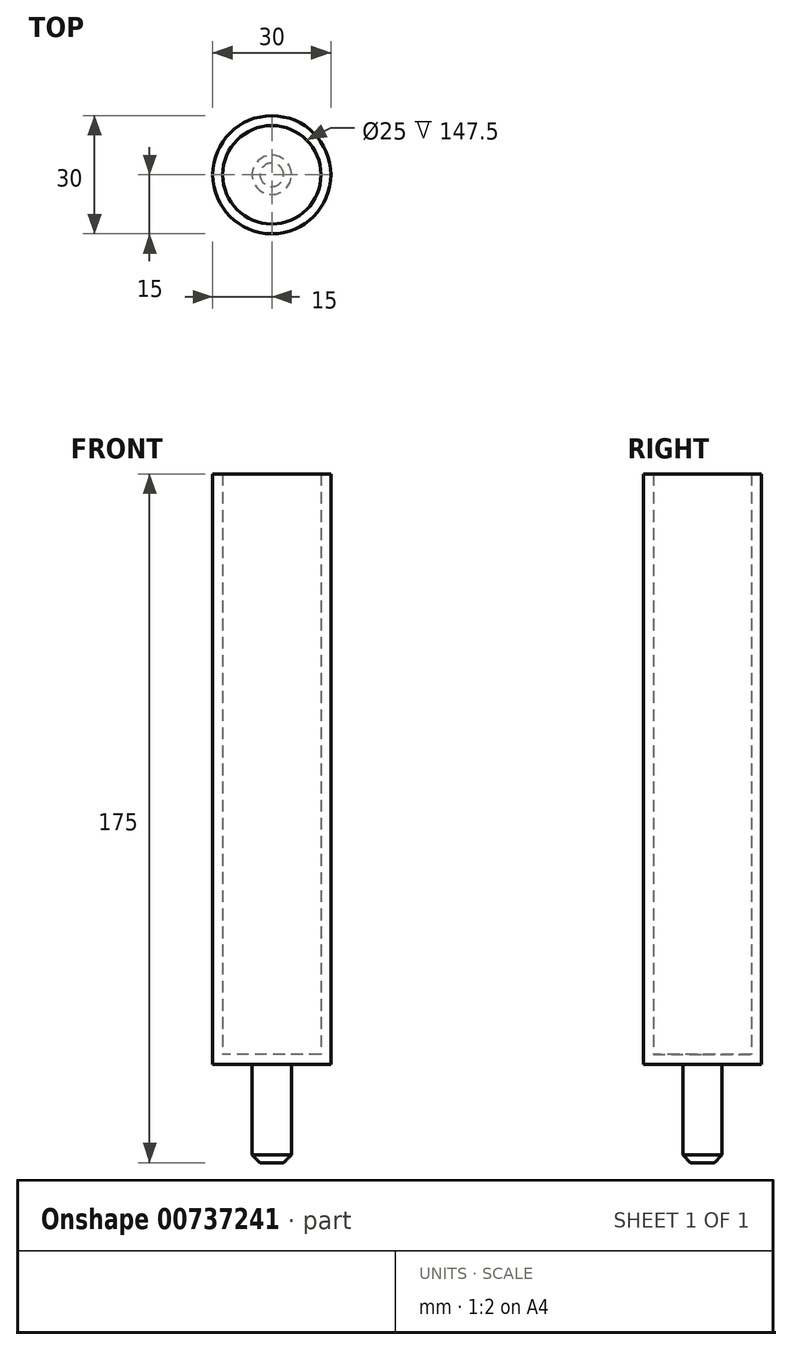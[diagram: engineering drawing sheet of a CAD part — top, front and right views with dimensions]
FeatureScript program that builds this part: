
annotation { "Feature Type Name" : "Feature", "Feature Type Description" : "" }
export const myFeature = defineFeature(function(context is Context, id is Id, definition is map)
    precondition{}
    {
        {
            var Q0;
            Q0=qCreatedBy(makeId("Top.planeOp"),FACE);
            var sketch = newSketch(context, id + "F0", { "sketchPlane" : qUnion([Q0])});
            skCircle(sketch, "E0", {"center": v(0, 0) * mm, "radius": 15 * mm});
            skSolve(sketch);
        }
        {
            var Q0;
            Q0=makeQuery(id+"F0.imprint","IMPRINT",FACE,{"disambiguationData":[TD([[makeQuery(id+"F0.imprint","IMPRINT",EDGE,{"derivedFrom":sQuery(id+"F0.wireOp",EDGE,"E0")}),1.0]])]});
            extrude(context, id + "F1", {"entities" : qUnion([Q0]), "depth" : 150 * mm, "offsetDistance" : 25 * mm});
        }
        {
            var Q0;
            Q0=makeQuery(id+"F1.opExtrude","CAP_FACE",FACE,{"disambiguationData":[OSD([sQuery(id+"F0.wireOp",EDGE,"E0")])],"isStart":false});
            shell(context, id + "F2", {"entities" : qUnion([Q0]), "thickness" : 2.5 * mm});
        }
        {
            var Q0;
            Q0=qCreatedBy(makeId("Top.planeOp"),FACE);
            var sketch = newSketch(context, id + "F3", { "sketchPlane" : qUnion([Q0])});
            skCircle(sketch, "E1", {"center": v(0, 0) * mm, "radius": 5 * mm});
            skSolve(sketch);
        }
        {
            var Q0;
            Q0=makeQuery(id+"F3.imprint","IMPRINT",FACE,{"disambiguationData":[TD([[makeQuery(id+"F3.imprint","IMPRINT",EDGE,{"derivedFrom":sQuery(id+"F3.wireOp",EDGE,"E1")}),1.0]])]});
            extrude(context, id + "F4", {"entities" : qUnion([Q0]), "operationType" : NewBodyOperationType.ADD, "oppositeDirection" : true, "depth" : 25 * mm, "offsetDistance" : 25 * mm});
        }
        {
            var Q0;
            Q0=makeQuery(id+"F4.opExtrude","CAP_EDGE",EDGE,{"disambiguationData":[OSD([sQuery(id+"F3.wireOp",EDGE,"E1")])],"isStart":false});
            chamfer(context, id + "F5", {"entities" : qUnion([Q0]), "width" : 2 * mm, "tangentPropagation" : true});
        }
    });
